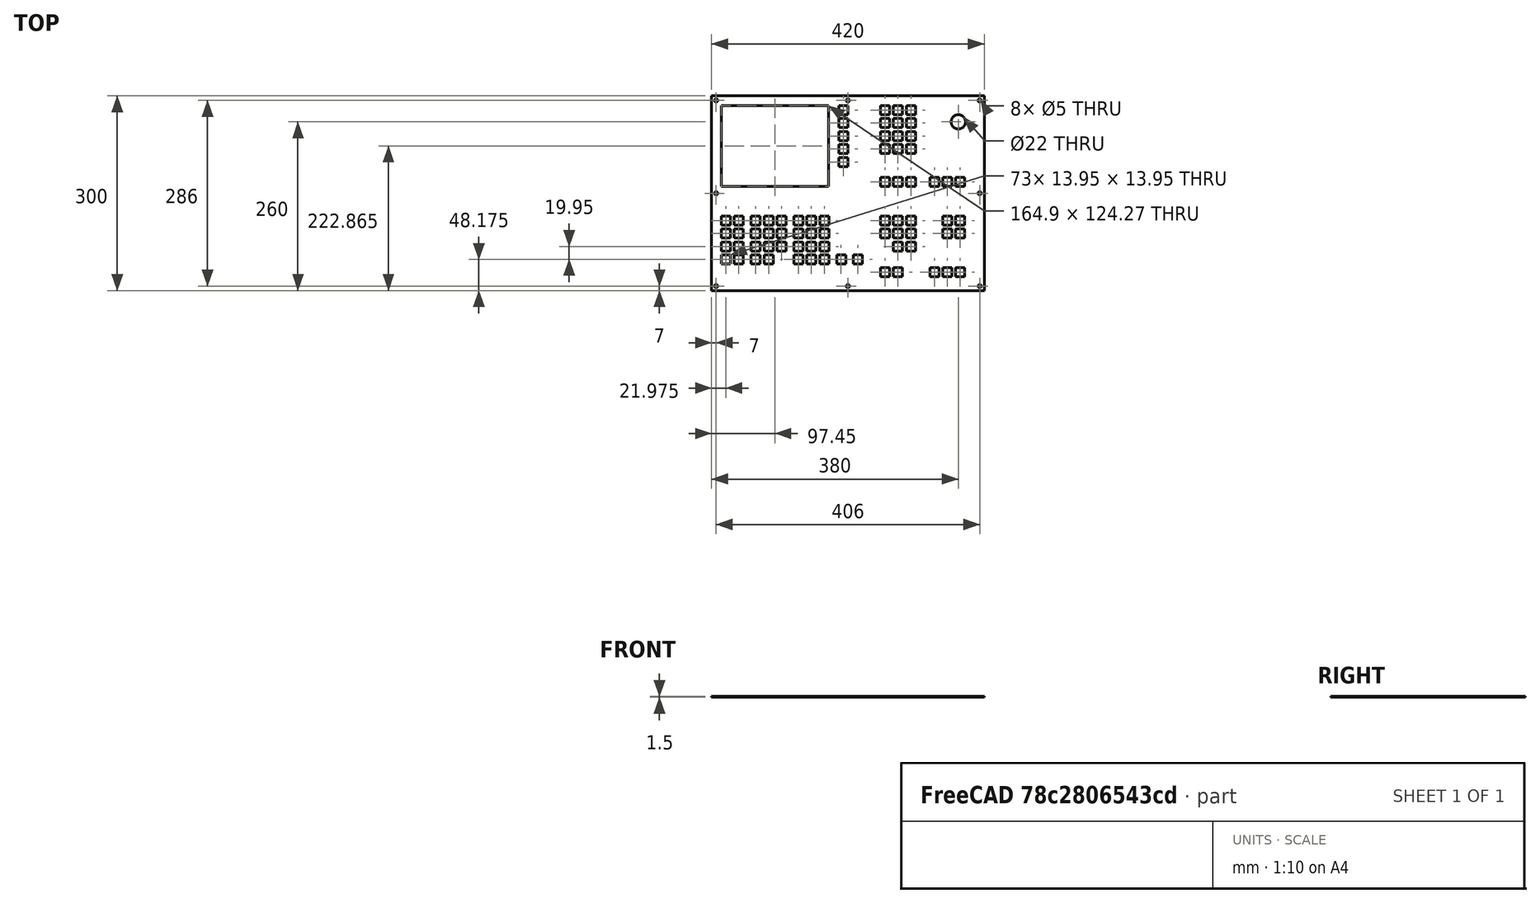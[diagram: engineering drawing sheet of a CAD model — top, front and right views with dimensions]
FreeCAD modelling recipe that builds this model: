
FCSTD DOCUMENT  (FreeCAD 0.20R26228 (Git))
Label: Hildi_Controller
License: All rights reserved
LicenseURL: http://en.wikipedia.org/wiki/All_rights_reserved
objects: Sketcher::SketchObject×1, Spreadsheet::Sheet×1, PartDesign::Pad×1, PartDesign::Body×1
note: 4 computed .brp shape members not serialized (recipe doc carries the construction recipe); baked Part::Feature solids carry a one-line shape summary decoded from their .brp

FEATURE [Sketcher::SketchObject] Sketch
  FullyConstrained = true
  MapMode = 5
  Support = -> [XY_Plane]
  expr: Constraints[229] = Spreadsheet.key_spacing
  expr: Constraints[421] = Spreadsheet.key_size
  expr: Constraints[445] = Spreadsheet.key_size
  expr: Constraints[417] = Spreadsheet.key_size
  expr: Constraints[439] = Spreadsheet.key_size
  expr: Constraints[416] = Spreadsheet.key_size
  expr: Constraints[625] = Spreadsheet.key_size
  expr: Constraints[169] = Spreadsheet.group_spacing
  expr: Constraints[440] = Spreadsheet.key_size
  expr: Constraints[450] = Spreadsheet.key_spacing
  expr: Constraints[414] = Spreadsheet.key_size
  expr: Constraints[219] = Spreadsheet.key_spacing
  expr: Constraints[144] = Spreadsheet.key_spacing
  expr: Constraints[626] = Spreadsheet.key_size
  expr: Constraints[415] = Spreadsheet.key_size
  expr: Constraints[220] = Spreadsheet.key_spacing
  expr: Constraints[230] = Spreadsheet.key_spacing
  expr: Constraints[865] = Spreadsheet.key_size
  expr: Constraints[624] = Spreadsheet.key_size
  expr: Constraints[285] = Spreadsheet.key_spacing
  expr: Constraints[443] = Spreadsheet.key_size
  expr: Constraints[278] = Spreadsheet.key_spacing
  expr: Constraints[233] = Spreadsheet.key_spacing
  expr: Constraints[442] = Spreadsheet.key_size
  expr: Constraints[769] = Spreadsheet.key_size
  expr: Constraints[299] = Spreadsheet.key_spacing
  expr: Constraints[915] = Spreadsheet.key_size
  expr: Constraints[623] = Spreadsheet.group_spacing
  expr: Constraints[493] = Spreadsheet.key_size
  expr: Constraints[300] = Spreadsheet.key_spacing
  expr: Constraints[494] = Spreadsheet.key_size
  expr: Constraints[444] = Spreadsheet.key_size
  expr: Constraints[446] = Spreadsheet.key_size
  expr: Constraints[221] = Spreadsheet.key_spacing
  expr: Constraints[635] = Spreadsheet.group_spacing
  expr: Constraints[143] = Spreadsheet.key_size
  expr: Constraints[422] = Spreadsheet.key_size
  expr: Constraints[567] = Spreadsheet.key_spacing
  expr: Constraints[218] = Spreadsheet.key_spacing
  expr: Constraints[566] = Spreadsheet.key_spacing
  expr: Constraints[639] = Spreadsheet.key_size
  expr: Constraints[418] = Spreadsheet.key_size
  expr: Constraints[863] = Spreadsheet.group_spacing
  expr: Constraints[495] = Spreadsheet.key_size
  expr: Constraints[922] = Spreadsheet.key_spacing
  expr: Constraints[780] = Spreadsheet.key_spacing
  expr: Constraints[441] = Spreadsheet.key_size
  expr: Constraints[496] = Spreadsheet.key_size
  expr: Constraints[925] = Spreadsheet.key_size
  sketch-geometry (309):
    g0: LineSegment StartX=-210 StartY=150 StartZ=0 EndX=210 EndY=150 EndZ=0
    g1: LineSegment StartX=210 StartY=150 StartZ=0 EndX=210 EndY=-150 EndZ=0
    g2: LineSegment StartX=210 StartY=-150 StartZ=0 EndX=-210 EndY=-150 EndZ=0
    g3: LineSegment StartX=-210 StartY=-150 StartZ=0 EndX=-210 EndY=150 EndZ=0
    g4: LineSegment StartX=-195 StartY=135 StartZ=0 EndX=-30.1 EndY=135 EndZ=0
    g5: LineSegment StartX=-30.1 StartY=135 StartZ=0 EndX=-30.1 EndY=10.73 EndZ=0
    g6: LineSegment StartX=-30.1 StartY=10.73 StartZ=0 EndX=-195 EndY=10.73 EndZ=0
    g7: LineSegment StartX=-195 StartY=10.73 StartZ=0 EndX=-195 EndY=135 EndZ=0
    g8: Circle CenterX=170 CenterY=110 CenterZ=0 NormalX=0 NormalY=0 NormalZ=1 AngleXU=0 Radius=11
    g9: LineSegment StartX=-195 StartY=-35 StartZ=0 EndX=-181.05 EndY=-35 EndZ=0
    g10: LineSegment StartX=-181.05 StartY=-35 StartZ=0 EndX=-181.05 EndY=-48.95 EndZ=0
    g11: LineSegment StartX=-181.05 StartY=-48.95 StartZ=0 EndX=-195 EndY=-48.95 EndZ=0
    g12: LineSegment StartX=-195 StartY=-48.95 StartZ=0 EndX=-195 EndY=-35 EndZ=0
    g13: LineSegment StartX=-195 StartY=-54.95 StartZ=0 EndX=-181.05 EndY=-54.95 EndZ=0
    g14: LineSegment StartX=-181.05 StartY=-54.95 StartZ=0 EndX=-181.05 EndY=-68.9 EndZ=0
    g15: LineSegment StartX=-181.05 StartY=-68.9 StartZ=0 EndX=-195 EndY=-68.9 EndZ=0
    g16: LineSegment StartX=-195 StartY=-68.9 StartZ=0 EndX=-195 EndY=-54.95 EndZ=0
    g17: LineSegment StartX=-195 StartY=-74.9 StartZ=0 EndX=-181.05 EndY=-74.9 EndZ=0
    g18: LineSegment StartX=-181.05 StartY=-74.9 StartZ=0 EndX=-181.05 EndY=-88.85 EndZ=0
    g19: LineSegment StartX=-181.05 StartY=-88.85 StartZ=0 EndX=-195 EndY=-88.85 EndZ=0
    g20: LineSegment StartX=-195 StartY=-88.85 StartZ=0 EndX=-195 EndY=-74.9 EndZ=0
    g21: LineSegment StartX=-195 StartY=-94.85 StartZ=0 EndX=-181.05 EndY=-94.85 EndZ=0
    g22: LineSegment StartX=-181.05 StartY=-94.85 StartZ=0 EndX=-181.05 EndY=-108.8 EndZ=0
    g23: LineSegment StartX=-181.05 StartY=-108.8 StartZ=0 EndX=-195 EndY=-108.8 EndZ=0
    g24: LineSegment StartX=-195 StartY=-108.8 StartZ=0 EndX=-195 EndY=-94.85 EndZ=0
    g25: LineSegment StartX=-175.05 StartY=-35 StartZ=0 EndX=-161.1 EndY=-35 EndZ=0
    g26: LineSegment StartX=-161.1 StartY=-35 StartZ=0 EndX=-161.1 EndY=-48.95 EndZ=0
    g27: LineSegment StartX=-161.1 StartY=-48.95 StartZ=0 EndX=-175.05 EndY=-48.95 EndZ=0
    g28: LineSegment StartX=-175.05 StartY=-48.95 StartZ=0 EndX=-175.05 EndY=-35 EndZ=0
    g29: LineSegment StartX=-175.05 StartY=-54.95 StartZ=0 EndX=-161.1 EndY=-54.95 EndZ=0
    g30: LineSegment StartX=-161.1 StartY=-54.95 StartZ=0 EndX=-161.1 EndY=-68.9 EndZ=0
    g31: LineSegment StartX=-161.1 StartY=-68.9 StartZ=0 EndX=-175.05 EndY=-68.9 EndZ=0
    g32: LineSegment StartX=-175.05 StartY=-68.9 StartZ=0 EndX=-175.05 EndY=-54.95 EndZ=0
    g33: LineSegment StartX=-175.05 StartY=-74.9 StartZ=0 EndX=-161.1 EndY=-74.9 EndZ=0
    g34: LineSegment StartX=-161.1 StartY=-74.9 StartZ=0 EndX=-161.1 EndY=-88.85 EndZ=0
    g35: LineSegment StartX=-161.1 StartY=-88.85 StartZ=0 EndX=-175.05 EndY=-88.85 EndZ=0
    g36: LineSegment StartX=-175.05 StartY=-88.85 StartZ=0 EndX=-175.05 EndY=-74.9 EndZ=0
    g37: LineSegment StartX=-175.05 StartY=-94.85 StartZ=0 EndX=-161.1 EndY=-94.85 EndZ=0
    g38: LineSegment StartX=-161.1 StartY=-94.85 StartZ=0 EndX=-161.1 EndY=-108.8 EndZ=0
    g39: LineSegment StartX=-161.1 StartY=-108.8 StartZ=0 EndX=-175.05 EndY=-108.8 EndZ=0
    g40: LineSegment StartX=-175.05 StartY=-108.8 StartZ=0 EndX=-175.05 EndY=-94.85 EndZ=0
    g41: LineSegment StartX=-149.1 StartY=-35 StartZ=0 EndX=-135.15 EndY=-35 EndZ=0
    g42: LineSegment StartX=-135.15 StartY=-35 StartZ=0 EndX=-135.15 EndY=-48.95 EndZ=0
    g43: LineSegment StartX=-135.15 StartY=-48.95 StartZ=0 EndX=-149.1 EndY=-48.95 EndZ=0
    g44: LineSegment StartX=-149.1 StartY=-48.95 StartZ=0 EndX=-149.1 EndY=-35 EndZ=0
    g45: LineSegment StartX=-129.15 StartY=-35 StartZ=0 EndX=-115.2 EndY=-35 EndZ=0
    g46: LineSegment StartX=-115.2 StartY=-35 StartZ=0 EndX=-115.2 EndY=-48.95 EndZ=0
    g47: LineSegment StartX=-115.2 StartY=-48.95 StartZ=0 EndX=-129.15 EndY=-48.95 EndZ=0
    g48: LineSegment StartX=-129.15 StartY=-48.95 StartZ=0 EndX=-129.15 EndY=-35 EndZ=0
    g49: LineSegment StartX=-149.1 StartY=-54.95 StartZ=0 EndX=-135.15 EndY=-54.95 EndZ=0
    g50: LineSegment StartX=-135.15 StartY=-54.95 StartZ=0 EndX=-135.15 EndY=-68.9 EndZ=0
    g51: LineSegment StartX=-135.15 StartY=-68.9 StartZ=0 EndX=-149.1 EndY=-68.9 EndZ=0
    g52: LineSegment StartX=-149.1 StartY=-68.9 StartZ=0 EndX=-149.1 EndY=-54.95 EndZ=0
    g53: LineSegment StartX=-129.15 StartY=-54.95 StartZ=0 EndX=-115.2 EndY=-54.95 EndZ=0
    g54: LineSegment StartX=-115.2 StartY=-54.95 StartZ=0 EndX=-115.2 EndY=-68.9 EndZ=0
    g55: LineSegment StartX=-115.2 StartY=-68.9 StartZ=0 EndX=-129.15 EndY=-68.9 EndZ=0
    g56: LineSegment StartX=-129.15 StartY=-68.9 StartZ=0 EndX=-129.15 EndY=-54.95 EndZ=0
    g57: LineSegment StartX=-109.2 StartY=-54.95 StartZ=0 EndX=-95.25 EndY=-54.95 EndZ=0
    g58: LineSegment StartX=-95.25 StartY=-54.95 StartZ=0 EndX=-95.25 EndY=-68.9 EndZ=0
    g59: LineSegment StartX=-95.25 StartY=-68.9 StartZ=0 EndX=-109.2 EndY=-68.9 EndZ=0
    g60: LineSegment StartX=-109.2 StartY=-68.9 StartZ=0 EndX=-109.2 EndY=-54.95 EndZ=0
    g61: LineSegment StartX=-149.1 StartY=-74.9 StartZ=0 EndX=-135.15 EndY=-74.9 EndZ=0
    g62: LineSegment StartX=-135.15 StartY=-74.9 StartZ=0 EndX=-135.15 EndY=-88.85 EndZ=0
    g63: LineSegment StartX=-135.15 StartY=-88.85 StartZ=0 EndX=-149.1 EndY=-88.85 EndZ=0
    g64: LineSegment StartX=-149.1 StartY=-88.85 StartZ=0 EndX=-149.1 EndY=-74.9 EndZ=0
    g65: LineSegment StartX=-129.15 StartY=-74.9 StartZ=0 EndX=-115.2 EndY=-74.9 EndZ=0
    g66: LineSegment StartX=-115.2 StartY=-74.9 StartZ=0 EndX=-115.2 EndY=-88.85 EndZ=0
    g67: LineSegment StartX=-115.2 StartY=-88.85 StartZ=0 EndX=-129.15 EndY=-88.85 EndZ=0
    g68: LineSegment StartX=-129.15 StartY=-88.85 StartZ=0 EndX=-129.15 EndY=-74.9 EndZ=0
    g69: LineSegment StartX=-109.2 StartY=-74.9 StartZ=0 EndX=-95.25 EndY=-74.9 EndZ=0
    g70: LineSegment StartX=-95.25 StartY=-74.9 StartZ=0 EndX=-95.25 EndY=-88.85 EndZ=0
    g71: LineSegment StartX=-95.25 StartY=-88.85 StartZ=0 EndX=-109.2 EndY=-88.85 EndZ=0
    g72: LineSegment StartX=-109.2 StartY=-88.85 StartZ=0 EndX=-109.2 EndY=-74.9 EndZ=0
    g73: LineSegment StartX=50 StartY=135 StartZ=0 EndX=63.95 EndY=135 EndZ=0
    g74: LineSegment StartX=63.95 StartY=135 StartZ=0 EndX=63.95 EndY=121.05 EndZ=0
    g75: LineSegment StartX=63.95 StartY=121.05 StartZ=0 EndX=50 EndY=121.05 EndZ=0
    g76: LineSegment StartX=50 StartY=121.05 StartZ=0 EndX=50 EndY=135 EndZ=0
    g77: LineSegment StartX=69.95 StartY=135 StartZ=0 EndX=83.9 EndY=135 EndZ=0
    g78: LineSegment StartX=83.9 StartY=135 StartZ=0 EndX=83.9 EndY=121.05 EndZ=0
    g79: LineSegment StartX=83.9 StartY=121.05 StartZ=0 EndX=69.95 EndY=121.05 EndZ=0
    g80: LineSegment StartX=69.95 StartY=121.05 StartZ=0 EndX=69.95 EndY=135 EndZ=0
    g81: LineSegment StartX=89.9 StartY=135 StartZ=0 EndX=103.85 EndY=135 EndZ=0
    g82: LineSegment StartX=103.85 StartY=135 StartZ=0 EndX=103.85 EndY=121.05 EndZ=0
    g83: LineSegment StartX=103.85 StartY=121.05 StartZ=0 EndX=89.9 EndY=121.05 EndZ=0
    g84: LineSegment StartX=89.9 StartY=121.05 StartZ=0 EndX=89.9 EndY=135 EndZ=0
    g85: LineSegment StartX=63.95 StartY=115.05 StartZ=0 EndX=50 EndY=115.05 EndZ=0
    g86: LineSegment StartX=50 StartY=115.05 StartZ=0 EndX=50 EndY=101.1 EndZ=0
    g87: LineSegment StartX=50 StartY=101.1 StartZ=0 EndX=63.95 EndY=101.1 EndZ=0
    g88: LineSegment StartX=63.95 StartY=101.1 StartZ=0 EndX=63.95 EndY=115.05 EndZ=0
    g89: LineSegment StartX=69.95 StartY=115.05 StartZ=0 EndX=83.9 EndY=115.05 EndZ=0
    g90: LineSegment StartX=83.9 StartY=115.05 StartZ=0 EndX=83.9 EndY=101.1 EndZ=0
    g91: LineSegment StartX=83.9 StartY=101.1 StartZ=0 EndX=69.95 EndY=101.1 EndZ=0
    g92: LineSegment StartX=69.95 StartY=101.1 StartZ=0 EndX=69.95 EndY=115.05 EndZ=0
    g93: LineSegment StartX=89.9 StartY=115.05 StartZ=0 EndX=103.85 EndY=115.05 EndZ=0
    g94: LineSegment StartX=103.85 StartY=115.05 StartZ=0 EndX=103.85 EndY=101.1 EndZ=0
    g95: LineSegment StartX=103.85 StartY=101.1 StartZ=0 EndX=89.9 EndY=101.1 EndZ=0
    g96: LineSegment StartX=89.9 StartY=101.1 StartZ=0 EndX=89.9 EndY=115.05 EndZ=0
    g97: LineSegment StartX=50 StartY=95.1 StartZ=0 EndX=63.95 EndY=95.1 EndZ=0
    g98: LineSegment StartX=63.95 StartY=95.1 StartZ=0 EndX=63.95 EndY=81.15 EndZ=0
    g99: LineSegment StartX=63.95 StartY=81.15 StartZ=0 EndX=50 EndY=81.15 EndZ=0
    g100: LineSegment StartX=50 StartY=81.15 StartZ=0 EndX=50 EndY=95.1 EndZ=0
    g101: LineSegment StartX=69.95 StartY=95.1 StartZ=0 EndX=83.9 EndY=95.1 EndZ=0
    g102: LineSegment StartX=83.9 StartY=95.1 StartZ=0 EndX=83.9 EndY=81.15 EndZ=0
    g103: LineSegment StartX=83.9 StartY=81.15 StartZ=0 EndX=69.95 EndY=81.15 EndZ=0
    g104: LineSegment StartX=69.95 StartY=81.15 StartZ=0 EndX=69.95 EndY=95.1 EndZ=0
    g105: LineSegment StartX=89.9 StartY=95.1 StartZ=0 EndX=103.85 EndY=95.1 EndZ=0
    g106: LineSegment StartX=103.85 StartY=95.1 StartZ=0 EndX=103.85 EndY=81.15 EndZ=0
    g107: LineSegment StartX=103.85 StartY=81.15 StartZ=0 EndX=89.9 EndY=81.15 EndZ=0
    g108: LineSegment StartX=89.9 StartY=81.15 StartZ=0 EndX=89.9 EndY=95.1 EndZ=0
    g109: LineSegment StartX=50 StartY=75.15 StartZ=0 EndX=63.95 EndY=75.15 EndZ=0
    g110: LineSegment StartX=63.95 StartY=75.15 StartZ=0 EndX=63.95 EndY=61.2 EndZ=0
    g111: LineSegment StartX=69.95 StartY=75.15 StartZ=0 EndX=83.9 EndY=75.15 EndZ=0
    g112: LineSegment StartX=83.9 StartY=75.15 StartZ=0 EndX=83.9 EndY=61.2 EndZ=0
    g113: LineSegment StartX=83.9 StartY=61.2 StartZ=0 EndX=69.95 EndY=61.2 EndZ=0
    g114: LineSegment StartX=69.95 StartY=61.2 StartZ=0 EndX=69.95 EndY=75.15 EndZ=0
    g115: LineSegment StartX=89.9 StartY=75.15 StartZ=0 EndX=103.85 EndY=75.15 EndZ=0
    g116: LineSegment StartX=103.85 StartY=75.15 StartZ=0 EndX=103.85 EndY=61.2 EndZ=0
    g117: LineSegment StartX=103.85 StartY=61.2 StartZ=0 EndX=89.9 EndY=61.2 EndZ=0
    g118: LineSegment StartX=89.9 StartY=61.2 StartZ=0 EndX=89.9 EndY=75.15 EndZ=0
    g119: LineSegment StartX=180 StartY=-114.8 StartZ=0 EndX=166.05 EndY=-114.8 EndZ=0
    g120: LineSegment StartX=166.05 StartY=-114.8 StartZ=0 EndX=166.05 EndY=-128.75 EndZ=0
    g121: LineSegment StartX=166.05 StartY=-128.75 StartZ=0 EndX=180 EndY=-128.75 EndZ=0
    g122: LineSegment StartX=180 StartY=-128.75 StartZ=0 EndX=180 EndY=-114.8 EndZ=0
    g123: LineSegment StartX=160.05 StartY=-114.8 StartZ=0 EndX=146.1 EndY=-114.8 EndZ=0
    g124: LineSegment StartX=146.1 StartY=-114.8 StartZ=0 EndX=146.1 EndY=-128.75 EndZ=0
    g125: LineSegment StartX=146.1 StartY=-128.75 StartZ=0 EndX=160.05 EndY=-128.75 EndZ=0
    g126: LineSegment StartX=160.05 StartY=-128.75 StartZ=0 EndX=160.05 EndY=-114.8 EndZ=0
    g127: LineSegment StartX=140.1 StartY=-114.8 StartZ=0 EndX=126.15 EndY=-114.8 EndZ=0
    g128: LineSegment StartX=126.15 StartY=-114.8 StartZ=0 EndX=126.15 EndY=-128.75 EndZ=0
    g129: LineSegment StartX=126.15 StartY=-128.75 StartZ=0 EndX=140.1 EndY=-128.75 EndZ=0
    g130: LineSegment StartX=140.1 StartY=-128.75 StartZ=0 EndX=140.1 EndY=-114.8 EndZ=0
    g131: LineSegment StartX=63.95 StartY=-48.95 StartZ=0 EndX=63.95 EndY=-35 EndZ=0
    g132: LineSegment StartX=63.95 StartY=-35 StartZ=0 EndX=50 EndY=-35 EndZ=0
    g133: LineSegment StartX=103.85 StartY=-54.95 StartZ=0 EndX=89.9 EndY=-54.95 EndZ=0
    g134: LineSegment StartX=89.9 StartY=-54.95 StartZ=0 EndX=89.9 EndY=-68.9 EndZ=0
    g135: LineSegment StartX=89.9 StartY=-68.9 StartZ=0 EndX=103.85 EndY=-68.9 EndZ=0
    g136: LineSegment StartX=103.85 StartY=-68.9 StartZ=0 EndX=103.85 EndY=-54.95 EndZ=0
    g137: LineSegment StartX=83.9 StartY=-54.95 StartZ=0 EndX=69.95 EndY=-54.95 EndZ=0
    g138: LineSegment StartX=69.95 StartY=-54.95 StartZ=0 EndX=69.95 EndY=-68.9 EndZ=0
    g139: LineSegment StartX=69.95 StartY=-68.9 StartZ=0 EndX=83.9 EndY=-68.9 EndZ=0
    g140: LineSegment StartX=83.9 StartY=-68.9 StartZ=0 EndX=83.9 EndY=-54.95 EndZ=0
    g141: LineSegment StartX=63.95 StartY=-54.95 StartZ=0 EndX=50 EndY=-54.95 EndZ=0
    g142: LineSegment StartX=50 StartY=-54.95 StartZ=0 EndX=50 EndY=-68.9 EndZ=0
    g143: LineSegment StartX=50 StartY=-68.9 StartZ=0 EndX=63.95 EndY=-68.9 EndZ=0
    g144: LineSegment StartX=63.95 StartY=-68.9 StartZ=0 EndX=63.95 EndY=-54.95 EndZ=0
    g145: LineSegment StartX=83.9 StartY=-48.95 StartZ=0 EndX=83.9 EndY=-35 EndZ=0
    g146: LineSegment StartX=83.9 StartY=-35 StartZ=0 EndX=69.95 EndY=-35 EndZ=0
    g147: LineSegment StartX=69.95 StartY=-74.9 StartZ=0 EndX=83.9 EndY=-74.9 EndZ=0
    g148: LineSegment StartX=83.9 StartY=-74.9 StartZ=0 EndX=83.9 EndY=-88.85 EndZ=0
    g149: LineSegment StartX=83.9 StartY=-88.85 StartZ=0 EndX=69.95 EndY=-88.85 EndZ=0
    g150: LineSegment StartX=69.95 StartY=-88.85 StartZ=0 EndX=69.95 EndY=-74.9 EndZ=0
    g151: LineSegment StartX=-17.4 StartY=-94.85 StartZ=0 EndX=-3.45 EndY=-94.85 EndZ=0
    g152: LineSegment StartX=-3.45 StartY=-94.85 StartZ=0 EndX=-3.45 EndY=-108.8 EndZ=0
    g153: LineSegment StartX=-3.45 StartY=-108.8 StartZ=0 EndX=-17.4 EndY=-108.8 EndZ=0
    g154: LineSegment StartX=-17.4 StartY=-108.8 StartZ=0 EndX=-17.4 EndY=-94.85 EndZ=0
    g155: Circle CenterX=-203 CenterY=143 CenterZ=0 NormalX=0 NormalY=0 NormalZ=1 AngleXU=0 Radius=2.5
    g156: Circle CenterX=-203 CenterY=0 CenterZ=0 NormalX=0 NormalY=0 NormalZ=1 AngleXU=0 Radius=2.5
    g157: Circle CenterX=-203 CenterY=-143 CenterZ=0 NormalX=0 NormalY=0 NormalZ=1 AngleXU=0 Radius=2.5
    g158: Circle CenterX=203 CenterY=-143 CenterZ=0 NormalX=0 NormalY=0 NormalZ=1 AngleXU=0 Radius=2.5
    g159: Circle CenterX=203 CenterY=0 CenterZ=0 NormalX=0 NormalY=0 NormalZ=1 AngleXU=0 Radius=2.5
    g160: Circle CenterX=203 CenterY=143 CenterZ=0 NormalX=0 NormalY=0 NormalZ=1 AngleXU=0 Radius=2.5
    g161: LineSegment StartX=89.9 StartY=-35 StartZ=0 EndX=103.85 EndY=-35 EndZ=0
    g162: LineSegment StartX=103.85 StartY=-35 StartZ=0 EndX=103.85 EndY=-48.95 EndZ=0
    g163: LineSegment StartX=103.85 StartY=-48.95 StartZ=0 EndX=89.9 EndY=-48.95 EndZ=0
    g164: LineSegment StartX=89.9 StartY=-48.95 StartZ=0 EndX=89.9 EndY=-35 EndZ=0
    g165: LineSegment StartX=89.9 StartY=-74.9 StartZ=0 EndX=103.85 EndY=-74.9 EndZ=0
    g166: LineSegment StartX=103.85 StartY=-74.9 StartZ=0 EndX=103.85 EndY=-88.85 EndZ=0
    g167: LineSegment StartX=103.85 StartY=-88.85 StartZ=0 EndX=89.9 EndY=-88.85 EndZ=0
    g168: LineSegment StartX=89.9 StartY=-88.85 StartZ=0 EndX=89.9 EndY=-74.9 EndZ=0
    g169: Circle CenterX=0 CenterY=-143 CenterZ=0 NormalX=0 NormalY=0 NormalZ=1 AngleXU=0 Radius=2.5
    g170: Circle CenterX=0 CenterY=143 CenterZ=0 NormalX=0 NormalY=0 NormalZ=1 AngleXU=0 Radius=2.5
    g171: LineSegment StartX=-129.15 StartY=-94.85 StartZ=0 EndX=-115.2 EndY=-94.85 EndZ=0
    g172: LineSegment StartX=-115.2 StartY=-94.85 StartZ=0 EndX=-115.2 EndY=-108.8 EndZ=0
    g173: LineSegment StartX=-115.2 StartY=-108.8 StartZ=0 EndX=-129.15 EndY=-108.8 EndZ=0
    g174: LineSegment StartX=-129.15 StartY=-108.8 StartZ=0 EndX=-129.15 EndY=-94.85 EndZ=0
    g175: LineSegment StartX=-109.2 StartY=-48.95 StartZ=0 EndX=-95.25 EndY=-48.95 EndZ=0
    g176: LineSegment StartX=-95.25 StartY=-48.95 StartZ=0 EndX=-95.25 EndY=-35 EndZ=0
    g177: LineSegment StartX=-95.25 StartY=-35 StartZ=0 EndX=-109.2 EndY=-35 EndZ=0
    g178: LineSegment StartX=-109.2 StartY=-35 StartZ=0 EndX=-109.2 EndY=-48.95 EndZ=0
    g179: LineSegment StartX=-149.1 StartY=-94.85 StartZ=0 EndX=-135.15 EndY=-94.85 EndZ=0
    g180: LineSegment StartX=-135.15 StartY=-94.85 StartZ=0 EndX=-135.15 EndY=-108.8 EndZ=0
    g181: LineSegment StartX=-135.15 StartY=-108.8 StartZ=0 EndX=-149.1 EndY=-108.8 EndZ=0
    g182: LineSegment StartX=-149.1 StartY=-108.8 StartZ=0 EndX=-149.1 EndY=-94.85 EndZ=0
    g183: LineSegment StartX=50 StartY=75.15 StartZ=0 EndX=50 EndY=61.2 EndZ=0
    g184: LineSegment StartX=50 StartY=61.2 StartZ=0 EndX=63.95 EndY=61.2 EndZ=0
    g185: LineSegment StartX=50 StartY=-35 StartZ=0 EndX=50 EndY=-48.95 EndZ=0
    g186: LineSegment StartX=50 StartY=-48.95 StartZ=0 EndX=63.95 EndY=-48.95 EndZ=0
    g187: LineSegment StartX=69.95 StartY=-35 StartZ=0 EndX=69.95 EndY=-48.95 EndZ=0
    g188: LineSegment StartX=69.95 StartY=-48.95 StartZ=0 EndX=83.9 EndY=-48.95 EndZ=0
    g189: LineSegment StartX=-83.25 StartY=-35 StartZ=0 EndX=-69.3 EndY=-35 EndZ=0
    g190: LineSegment StartX=-69.3 StartY=-35 StartZ=0 EndX=-69.3 EndY=-48.95 EndZ=0
    g191: LineSegment StartX=-69.3 StartY=-48.95 StartZ=0 EndX=-83.25 EndY=-48.95 EndZ=0
    g192: LineSegment StartX=-83.25 StartY=-48.95 StartZ=0 EndX=-83.25 EndY=-35 EndZ=0
    g193: LineSegment StartX=-63.3 StartY=-35 StartZ=0 EndX=-49.35 EndY=-35 EndZ=0
    g194: LineSegment StartX=-49.35 StartY=-35 StartZ=0 EndX=-49.35 EndY=-48.95 EndZ=0
    g195: LineSegment StartX=-49.35 StartY=-48.95 StartZ=0 EndX=-63.3 EndY=-48.95 EndZ=0
    g196: LineSegment StartX=-63.3 StartY=-48.95 StartZ=0 EndX=-63.3 EndY=-35 EndZ=0
    g197: LineSegment StartX=-83.25 StartY=-54.95 StartZ=0 EndX=-69.3 EndY=-54.95 EndZ=0
    g198: LineSegment StartX=-69.3 StartY=-54.95 StartZ=0 EndX=-69.3 EndY=-68.9 EndZ=0
    g199: LineSegment StartX=-69.3 StartY=-68.9 StartZ=0 EndX=-83.25 EndY=-68.9 EndZ=0
    g200: LineSegment StartX=-83.25 StartY=-68.9 StartZ=0 EndX=-83.25 EndY=-54.95 EndZ=0
    g201: LineSegment StartX=-63.3 StartY=-54.95 StartZ=0 EndX=-49.35 EndY=-54.95 EndZ=0
    g202: LineSegment StartX=-49.35 StartY=-54.95 StartZ=0 EndX=-49.35 EndY=-68.9 EndZ=0
    g203: LineSegment StartX=-49.35 StartY=-68.9 StartZ=0 EndX=-63.3 EndY=-68.9 EndZ=0
    g204: LineSegment StartX=-63.3 StartY=-68.9 StartZ=0 EndX=-63.3 EndY=-54.95 EndZ=0
    g205: LineSegment StartX=-43.35 StartY=-54.95 StartZ=0 EndX=-29.4 EndY=-54.95 EndZ=0
    g206: LineSegment StartX=-29.4 StartY=-54.95 StartZ=0 EndX=-29.4 EndY=-68.9 EndZ=0
    g207: LineSegment StartX=-29.4 StartY=-68.9 StartZ=0 EndX=-43.35 EndY=-68.9 EndZ=0
    g208: LineSegment StartX=-43.35 StartY=-68.9 StartZ=0 EndX=-43.35 EndY=-54.95 EndZ=0
    g209: LineSegment StartX=-83.25 StartY=-74.9 StartZ=0 EndX=-69.3 EndY=-74.9 EndZ=0
    g210: LineSegment StartX=-69.3 StartY=-74.9 StartZ=0 EndX=-69.3 EndY=-88.85 EndZ=0
    g211: LineSegment StartX=-69.3 StartY=-88.85 StartZ=0 EndX=-83.25 EndY=-88.85 EndZ=0
    g212: LineSegment StartX=-83.25 StartY=-88.85 StartZ=0 EndX=-83.25 EndY=-74.9 EndZ=0
    g213: LineSegment StartX=-63.3 StartY=-74.9 StartZ=0 EndX=-49.35 EndY=-74.9 EndZ=0
    g214: LineSegment StartX=-49.35 StartY=-74.9 StartZ=0 EndX=-49.35 EndY=-88.85 EndZ=0
    g215: LineSegment StartX=-49.35 StartY=-88.85 StartZ=0 EndX=-63.3 EndY=-88.85 EndZ=0
    g216: LineSegment StartX=-63.3 StartY=-88.85 StartZ=0 EndX=-63.3 EndY=-74.9 EndZ=0
    g217: LineSegment StartX=-43.35 StartY=-74.9 StartZ=0 EndX=-29.4 EndY=-74.9 EndZ=0
    g218: LineSegment StartX=-29.4 StartY=-74.9 StartZ=0 EndX=-29.4 EndY=-88.85 EndZ=0
    g219: LineSegment StartX=-29.4 StartY=-88.85 StartZ=0 EndX=-43.35 EndY=-88.85 EndZ=0
    g220: LineSegment StartX=-43.35 StartY=-88.85 StartZ=0 EndX=-43.35 EndY=-74.9 EndZ=0
    g221: LineSegment StartX=-63.3 StartY=-94.85 StartZ=0 EndX=-49.35 EndY=-94.85 EndZ=0
    g222: LineSegment StartX=-49.35 StartY=-94.85 StartZ=0 EndX=-49.35 EndY=-108.8 EndZ=0
    g223: LineSegment StartX=-49.35 StartY=-108.8 StartZ=0 EndX=-63.3 EndY=-108.8 EndZ=0
    g224: LineSegment StartX=-63.3 StartY=-108.8 StartZ=0 EndX=-63.3 EndY=-94.85 EndZ=0
    g225: LineSegment StartX=-43.35 StartY=-48.95 StartZ=0 EndX=-29.4 EndY=-48.95 EndZ=0
    g226: LineSegment StartX=-29.4 StartY=-48.95 StartZ=0 EndX=-29.4 EndY=-35 EndZ=0
    g227: LineSegment StartX=-29.4 StartY=-35 StartZ=0 EndX=-43.35 EndY=-35 EndZ=0
    g228: LineSegment StartX=-43.35 StartY=-35 StartZ=0 EndX=-43.35 EndY=-48.95 EndZ=0
    g229: LineSegment StartX=-83.25 StartY=-94.85 StartZ=0 EndX=-69.3 EndY=-94.85 EndZ=0
    g230: LineSegment StartX=-69.3 StartY=-94.85 StartZ=0 EndX=-69.3 EndY=-108.8 EndZ=0
    g231: LineSegment StartX=-69.3 StartY=-108.8 StartZ=0 EndX=-83.25 EndY=-108.8 EndZ=0
    g232: LineSegment StartX=-83.25 StartY=-108.8 StartZ=0 EndX=-83.25 EndY=-94.85 EndZ=0
    g233: LineSegment StartX=50 StartY=-114.8 StartZ=0 EndX=63.95 EndY=-114.8 EndZ=0
    g234: LineSegment StartX=63.95 StartY=-114.8 StartZ=0 EndX=63.95 EndY=-128.75 EndZ=0
    g235: LineSegment StartX=63.95 StartY=-128.75 StartZ=0 EndX=50 EndY=-128.75 EndZ=0
    g236: LineSegment StartX=50 StartY=-128.75 StartZ=0 EndX=50 EndY=-114.8 EndZ=0
    g237: LineSegment StartX=69.95 StartY=-114.8 StartZ=0 EndX=83.9 EndY=-114.8 EndZ=0
    g238: LineSegment StartX=83.9 StartY=-114.8 StartZ=0 EndX=83.9 EndY=-128.75 EndZ=0
    g239: LineSegment StartX=83.9 StartY=-128.75 StartZ=0 EndX=69.95 EndY=-128.75 EndZ=0
    g240: LineSegment StartX=69.95 StartY=-128.75 StartZ=0 EndX=69.95 EndY=-114.8 EndZ=0
    g241: LineSegment StartX=50 StartY=24.68 StartZ=0 EndX=63.95 EndY=24.68 EndZ=0
    g242: LineSegment StartX=63.95 StartY=24.68 StartZ=0 EndX=63.95 EndY=10.73 EndZ=0
    g243: LineSegment StartX=63.95 StartY=10.73 StartZ=0 EndX=50 EndY=10.73 EndZ=0
    g244: LineSegment StartX=50 StartY=10.73 StartZ=0 EndX=50 EndY=24.68 EndZ=0
    g245: LineSegment StartX=69.95 StartY=24.68 StartZ=0 EndX=83.9 EndY=24.68 EndZ=0
    g246: LineSegment StartX=83.9 StartY=24.68 StartZ=0 EndX=83.9 EndY=10.73 EndZ=0
    g247: LineSegment StartX=83.9 StartY=10.73 StartZ=0 EndX=69.95 EndY=10.73 EndZ=0
    g248: LineSegment StartX=69.95 StartY=10.73 StartZ=0 EndX=69.95 EndY=24.68 EndZ=0
    g249: LineSegment StartX=166.05 StartY=-68.9 StartZ=0 EndX=180 EndY=-68.9 EndZ=0
    g250: LineSegment StartX=180 StartY=-68.9 StartZ=0 EndX=180 EndY=-54.95 EndZ=0
    g251: LineSegment StartX=180 StartY=-54.95 StartZ=0 EndX=166.05 EndY=-54.95 EndZ=0
    g252: LineSegment StartX=166.05 StartY=-54.95 StartZ=0 EndX=166.05 EndY=-68.9 EndZ=0
    g253: LineSegment StartX=180 StartY=-35 StartZ=0 EndX=166.05 EndY=-35 EndZ=0
    g254: LineSegment StartX=166.05 StartY=-35 StartZ=0 EndX=166.05 EndY=-48.95 EndZ=0
    g255: LineSegment StartX=166.05 StartY=-48.95 StartZ=0 EndX=180 EndY=-48.95 EndZ=0
    g256: LineSegment StartX=180 StartY=-48.95 StartZ=0 EndX=180 EndY=-35 EndZ=0
    g257: LineSegment StartX=89.9 StartY=24.68 StartZ=0 EndX=103.85 EndY=24.68 EndZ=0
    g258: LineSegment StartX=103.85 StartY=24.68 StartZ=0 EndX=103.85 EndY=10.73 EndZ=0
    g259: LineSegment StartX=103.85 StartY=10.73 StartZ=0 EndX=89.9 EndY=10.73 EndZ=0
    g260: LineSegment StartX=89.9 StartY=10.73 StartZ=0 EndX=89.9 EndY=24.68 EndZ=0
    g261: LineSegment StartX=160.05 StartY=-35 StartZ=0 EndX=146.1 EndY=-35 EndZ=0
    g262: LineSegment StartX=146.1 StartY=-35 StartZ=0 EndX=146.1 EndY=-48.95 EndZ=0
    g263: LineSegment StartX=146.1 StartY=-48.95 StartZ=0 EndX=160.05 EndY=-48.95 EndZ=0
    g264: LineSegment StartX=160.05 StartY=-48.95 StartZ=0 EndX=160.05 EndY=-35 EndZ=0
    g265: LineSegment StartX=160.05 StartY=-54.95 StartZ=0 EndX=146.1 EndY=-54.95 EndZ=0
    g266: LineSegment StartX=146.1 StartY=-54.95 StartZ=0 EndX=146.1 EndY=-68.9 EndZ=0
    g267: LineSegment StartX=146.1 StartY=-68.9 StartZ=0 EndX=160.05 EndY=-68.9 EndZ=0
    g268: LineSegment StartX=160.05 StartY=-68.9 StartZ=0 EndX=160.05 EndY=-54.95 EndZ=0
    g269: LineSegment StartX=126.15 StartY=24.68 StartZ=0 EndX=140.1 EndY=24.68 EndZ=0
    g270: LineSegment StartX=140.1 StartY=24.68 StartZ=0 EndX=140.1 EndY=10.73 EndZ=0
    g271: LineSegment StartX=140.1 StartY=10.73 StartZ=0 EndX=126.15 EndY=10.73 EndZ=0
    g272: LineSegment StartX=126.15 StartY=10.73 StartZ=0 EndX=126.15 EndY=24.68 EndZ=0
    g273: LineSegment StartX=146.1 StartY=24.68 StartZ=0 EndX=160.05 EndY=24.68 EndZ=0
    g274: LineSegment StartX=160.05 StartY=24.68 StartZ=0 EndX=160.05 EndY=10.73 EndZ=0
    g275: LineSegment StartX=160.05 StartY=10.73 StartZ=0 EndX=146.1 EndY=10.73 EndZ=0
    g276: LineSegment StartX=146.1 StartY=10.73 StartZ=0 EndX=146.1 EndY=24.68 EndZ=0
    g277: LineSegment StartX=166.05 StartY=24.68 StartZ=0 EndX=180 EndY=24.68 EndZ=0
    g278: LineSegment StartX=180 StartY=24.68 StartZ=0 EndX=180 EndY=10.73 EndZ=0
    g279: LineSegment StartX=180 StartY=10.73 StartZ=0 EndX=166.05 EndY=10.73 EndZ=0
    g280: LineSegment StartX=166.05 StartY=10.73 StartZ=0 EndX=166.05 EndY=24.68 EndZ=0
    g281: LineSegment StartX=-43.35 StartY=-94.85 StartZ=0 EndX=-29.4 EndY=-94.85 EndZ=0
    g282: LineSegment StartX=-29.4 StartY=-94.85 StartZ=0 EndX=-29.4 EndY=-108.8 EndZ=0
    g283: LineSegment StartX=-29.4 StartY=-108.8 StartZ=0 EndX=-43.35 EndY=-108.8 EndZ=0
    g284: LineSegment StartX=-43.35 StartY=-108.8 StartZ=0 EndX=-43.35 EndY=-94.85 EndZ=0
    g285: LineSegment StartX=8.55 StartY=-94.85 StartZ=0 EndX=22.5 EndY=-94.85 EndZ=0
    g286: LineSegment StartX=22.5 StartY=-94.85 StartZ=0 EndX=22.5 EndY=-108.8 EndZ=0
    g287: LineSegment StartX=22.5 StartY=-108.8 StartZ=0 EndX=8.55 EndY=-108.8 EndZ=0
    g288: LineSegment StartX=8.55 StartY=-108.8 StartZ=0 EndX=8.55 EndY=-94.85 EndZ=0
    g289: LineSegment StartX=-13.95 StartY=135 StartZ=0 EndX=0 EndY=135 EndZ=0
    g290: LineSegment StartX=0 StartY=135 StartZ=0 EndX=0 EndY=121.05 EndZ=0
    g291: LineSegment StartX=0 StartY=121.05 StartZ=0 EndX=-13.95 EndY=121.05 EndZ=0
    g292: LineSegment StartX=-13.95 StartY=121.05 StartZ=0 EndX=-13.95 EndY=135 EndZ=0
    g293: LineSegment StartX=-13.95 StartY=115.05 StartZ=0 EndX=0 EndY=115.05 EndZ=0
    g294: LineSegment StartX=0 StartY=115.05 StartZ=0 EndX=0 EndY=101.1 EndZ=0
    g295: LineSegment StartX=0 StartY=101.1 StartZ=0 EndX=-13.95 EndY=101.1 EndZ=0
    g296: LineSegment StartX=-13.95 StartY=101.1 StartZ=0 EndX=-13.95 EndY=115.05 EndZ=0
    g297: LineSegment StartX=-13.95 StartY=95.1 StartZ=0 EndX=0 EndY=95.1 EndZ=0
    g298: LineSegment StartX=0 StartY=95.1 StartZ=0 EndX=0 EndY=81.15 EndZ=0
    g299: LineSegment StartX=0 StartY=81.15 StartZ=0 EndX=-13.95 EndY=81.15 EndZ=0
    g300: LineSegment StartX=-13.95 StartY=81.15 StartZ=0 EndX=-13.95 EndY=95.1 EndZ=0
    g301: LineSegment StartX=-13.95 StartY=75.15 StartZ=0 EndX=0 EndY=75.15 EndZ=0
    g302: LineSegment StartX=0 StartY=75.15 StartZ=0 EndX=0 EndY=61.2 EndZ=0
    g303: LineSegment StartX=0 StartY=61.2 StartZ=0 EndX=-13.95 EndY=61.2 EndZ=0
    g304: LineSegment StartX=-13.95 StartY=61.2 StartZ=0 EndX=-13.95 EndY=75.15 EndZ=0
    g305: LineSegment StartX=-13.95 StartY=55.2 StartZ=0 EndX=0 EndY=55.2 EndZ=0
    g306: LineSegment StartX=0 StartY=55.2 StartZ=0 EndX=0 EndY=41.25 EndZ=0
    g307: LineSegment StartX=0 StartY=41.25 StartZ=0 EndX=-13.95 EndY=41.25 EndZ=0
    g308: LineSegment StartX=-13.95 StartY=41.25 StartZ=0 EndX=-13.95 EndY=55.2 EndZ=0
  constraints (926):
    c: Coincident(g1,g2)
    c: Coincident(g2,g3)
    c: Coincident(g3,g0)
    c: DistanceY(g3,g3) = 300
    c: Coincident(g4,g5)
    c: Coincident(g5,g6)
    c: DistanceX(g4,g4) = 164.9
    c: DistanceY(g7,g7) = 124.27
    c: DistanceY(g4,g0) = 15
    c: Diameter(g8) = 22
    c: DistanceX(g8,g0) = 40
    c: DistanceY(g8,g0) = 40
    c: Coincident(g10,g11)
    c: Coincident(g11,g12)
    c: Coincident(g12,g9)
    c: Coincident(g13,g14)
    c: Coincident(g14,g15)
    c: Coincident(g15,g16)
    c: Coincident(g16,g13)
    c: Coincident(g17,g18)
    c: Coincident(g18,g19)
    c: Coincident(g19,g20)
    c: Coincident(g20,g17)
    c: Coincident(g21,g22)
    c: Coincident(g22,g23)
    c: Coincident(g23,g24)
    c: Coincident(g24,g21)
    c: Coincident(g25,g26)
    c: Coincident(g26,g27)
    c: Coincident(g29,g30)
    c: Coincident(g30,g31)
    c: Coincident(g31,g32)
    c: Coincident(g32,g29)
    c: Coincident(g33,g34)
    c: Coincident(g34,g35)
    c: Coincident(g35,g36)
    c: Coincident(g36,g33)
    c: Coincident(g37,g38)
    c: Coincident(g38,g39)
    c: Coincident(g39,g40)
    c: Coincident(g40,g37)
    c: Coincident(g42,g43)
    c: Coincident(g43,g44)
    c: Coincident(g44,g41)
    c: Coincident(g45,g46)
    c: Coincident(g46,g47)
    c: Coincident(g47,g48)
    c: Coincident(g48,g45)
    c: Coincident(g49,g50)
    c: Coincident(g50,g51)
    c: Coincident(g51,g52)
    c: Coincident(g52,g49)
    c: Coincident(g53,g54)
    c: Coincident(g54,g55)
    c: Coincident(g57,g58)
    c: Coincident(g58,g59)
    c: Coincident(g59,g60)
    c: Coincident(g60,g57)
    c: Coincident(g61,g62)
    c: Coincident(g62,g63)
    c: Coincident(g63,g64)
    c: Coincident(g64,g61)
    c: Coincident(g66,g67)
    c: Coincident(g67,g68)
    c: Coincident(g68,g65)
    c: Coincident(g70,g71)
    c: Coincident(g73,g74)
    c: Coincident(g74,g75)
    c: Coincident(g75,g76)
    c: Coincident(g76,g73)
    c: Coincident(g77,g78)
    c: Coincident(g78,g79)
    c: Coincident(g79,g80)
    c: Coincident(g80,g77)
    c: Coincident(g81,g82)
    c: Coincident(g82,g83)
    c: Coincident(g83,g84)
    c: Coincident(g84,g81)
    c: Coincident(g85,g86)
    c: Coincident(g86,g87)
    c: Coincident(g87,g88)
    c: Coincident(g88,g85)
    c: Coincident(g89,g90)
    c: Coincident(g90,g91)
    c: Coincident(g91,g92)
    c: Coincident(g92,g89)
    c: Coincident(g93,g94)
    c: Coincident(g94,g95)
    c: Coincident(g95,g96)
    c: Coincident(g96,g93)
    c: Coincident(g97,g98)
    c: Coincident(g98,g99)
    c: Coincident(g99,g100)
    c: Coincident(g100,g97)
    c: Coincident(g101,g102)
    c: Coincident(g102,g103)
    c: Coincident(g103,g104)
    c: Coincident(g105,g106)
    c: Coincident(g106,g107)
    c: Coincident(g107,g108)
    c: Coincident(g108,g105)
    c: Coincident(g109,g110)
    c: Coincident(g111,g112)
    c: Coincident(g112,g113)
    c: Coincident(g113,g114)
    c: Coincident(g114,g111)
    c: Coincident(g115,g116)
    c: Coincident(g116,g117)
    c: Coincident(g117,g118)
    c: Coincident(g118,g115)
    c: Coincident(g119,g120)
    c: Coincident(g120,g121)
    c: Coincident(g121,g122)
    c: Coincident(g122,g119)
    c: Coincident(g123,g124)
    c: Coincident(g124,g125)
    c: Coincident(g125,g126)
    c: Coincident(g126,g123)
    c: Coincident(g127,g128)
    c: Coincident(g128,g129)
    c: Coincident(g129,g130)
    c: Coincident(g130,g127)
    c: Coincident(g131,g132)
    c: Coincident(g133,g134)
    c: Coincident(g134,g135)
    c: Coincident(g135,g136)
    c: Coincident(g136,g133)
    c: Coincident(g137,g138)
    c: Coincident(g138,g139)
    c: Coincident(g139,g140)
    c: Coincident(g140,g137)
    c: Coincident(g141,g142)
    c: Coincident(g142,g143)
    c: Coincident(g143,g144)
    c: Coincident(g144,g141)
    c: Coincident(g145,g146)
    c: Coincident(g147,g148)
    c: Coincident(g148,g149)
    c: Coincident(g149,g150)
    c: Coincident(g150,g147)
    c: Coincident(g152,g153)
    c: Coincident(g153,g154)
    c: Coincident(g154,g151)
    c: DistanceY(g12,g12) = 13.95
    c: DistanceY(g13,g11) = 6
    c: DistanceX(g0,g155) = 7
    c: DistanceY(g155,g0) = 7
    c: Diameter(g155) = 5
    c: Coincident(g161,g162)
    c: Coincident(g162,g163)
    c: Coincident(g163,g164)
    c: Coincident(g164,g161)
    c: Coincident(g165,g166)
    c: Coincident(g166,g167)
    c: Coincident(g167,g168)
    c: Coincident(g168,g165)
    c: DistanceY(g2,g157) = 7
    c: DistanceX(g160,g0) = 7
    c: Coincident(g171,g172)
    c: Coincident(g172,g173)
    c: Coincident(g173,g174)
    c: Coincident(g174,g171)
    c: Coincident(g175,g176)
    c: Coincident(g176,g177)
    c: Coincident(g177,g178)
    c: Coincident(g178,g175)
    c: Coincident(g72,g69)
    c: Coincident(g66,g65)
    c: Coincident(g25,g28)
    c: DistanceX(g25,g41) = 12
    c: Coincident(g27,g28)
    c: Coincident(g70,g69)
    c: Coincident(g72,g71)
    c: Coincident(g152,g151)
    c: Coincident(g42,g41)
    c: Coincident(g10,g9)
    c: DistanceX(g0,g0) = 420
    c: Coincident(g179,g180)
    c: Coincident(g180,g181)
    c: Coincident(g181,g182)
    c: Coincident(g182,g179)
    c: Horizontal(g9)
    c: Horizontal(g25)
    c: Horizontal(g41)
    c: Horizontal(g45)
    c: Horizontal(g177)
    c: Horizontal(g0)
    c: Horizontal(g2)
    c: Horizontal(g13)
    c: Horizontal(g29)
    c: Horizontal(g49)
    c: Horizontal(g53)
    c: Horizontal(g57)
    c: Horizontal(g17)
    c: Horizontal(g33)
    c: Horizontal(g61)
    c: Horizontal(g65)
    c: Horizontal(g69)
    c: Horizontal(g21)
    c: Horizontal(g37)
    c: Horizontal(g171)
    c: Horizontal(g179)
    c: Vertical(g12)
    c: Vertical(g16)
    c: Vertical(g20)
    c: Vertical(g24)
    c: Vertical(g28)
    c: Vertical(g32)
    c: Vertical(g44)
    c: Vertical(g52)
    c: Vertical(g64)
    c: Vertical(g182)
    c: Vertical(g48)
    c: Vertical(g56)
    c: Vertical(g68)
    c: Vertical(g174)
    c: Vertical(g60)
    c: Vertical(g178)
    c: DistanceX(g41,g45) = 6
    c: DistanceX(g45,g177) = 6
    c: DistanceY(g17,g15) = 6
    c: DistanceY(g21,g19) = 6
    c: Horizontal(g4)
    c: Horizontal(g6)
    c: Vertical(g5)
    c: Vertical(g7)
    c: Vertical(g3)
    c: Vertical(g1)
    c: Horizontal(g81)
    c: DistanceX(g73,g77) = 6
    c: DistanceX(g77,g81) = 6
    c: Vertical(g76)
    c: Vertical(g86)
    c: DistanceY(g85,g75) = 6
    c: Horizontal(g73,g4)
    c: Vertical(g75,g85)
    c: Vertical(g180)
    c: Vertical(g11,g13)
    c: Vertical(g15,g17)
    c: Vertical(g19,g21)
    c: Vertical(g27,g29)
    c: Vertical(g31,g33)
    c: Vertical(g35,g37)
    c: Vertical(g43,g49)
    c: Vertical(g51,g61)
    c: Vertical(g63,g179)
    c: Vertical(g47,g53)
    c: Vertical(g55,g65)
    c: Vertical(g67,g171)
    c: Vertical(g175,g57)
    c: Vertical(g59,g69)
    c: Horizontal(g9,g25)
    c: Horizontal(g25,g41)
    c: Horizontal(g41,g45)
    c: Horizontal(g45,g177)
    c: Horizontal(g13,g29)
    c: Horizontal(g29,g49)
    c: Horizontal(g49,g53)
    c: Horizontal(g53,g57)
    c: Horizontal(g17,g33)
    c: Horizontal(g33,g61)
    c: Horizontal(g61,g65)
    c: Horizontal(g65,g69)
    c: Horizontal(g21,g37)
    c: Horizontal(g37,g179)
    c: Horizontal(g179,g171)
    c: Vertical(g78)
    c: Horizontal(g97)
    c: Horizontal(g109)
    c: Vertical(g86,g97)
    c: Vertical(g99,g109)
    c: Horizontal(g85,g89)
    c: Horizontal(g89,g93)
    c: Horizontal(g89)
    c: Horizontal(g107)
    c: Vertical(g94)
    c: Vertical(g110)
    c: Vertical(g118)
    c: DistanceY(g97,g86) = 6
    c: Vertical(g79,g89)
    c: Vertical(g91,g101)
    c: Vertical(g103,g111)
    c: Vertical(g83,g93)
    c: Vertical(g95,g105)
    c: Vertical(g107,g115)
    c: DistanceY(g109,g99) = 6
    c: Horizontal(g97,g101)
    c: Horizontal(g111,g109)
    c: Horizontal(g105,g101)
    c: Horizontal(g115,g111)
    c: Vertical(g155,g156)
    c: Vertical(g156,g157)
    c: Vertical(g160,g159)
    c: Vertical(g159,g158)
    c: Horizontal(g119)
    c: Vertical(g120)
    c: Vertical(g128)
    c: Horizontal(g127,g123)
    c: Horizontal(g123,g119)
    c: DistanceX(g127,g123) = 6
    c: DistanceX(g123,g119) = 6
    c: Horizontal(g141)
    c: Horizontal(g137)
    c: Horizontal(g147)
    c: Horizontal(g133)
    c: Horizontal(g161)
    c: Horizontal(g165)
    c: Vertical(g162)
    c: Vertical(g134)
    c: Vertical(g138)
    c: Vertical(g142)
    c: Vertical(g166)
    c: Coincident(g56,g53)
    c: Coincident(g55,g56)
    c: Coincident(g0,g1)
    c: Symmetric(g0,g1,g-1)
    c: DistanceX(g0,g7) = 15
    c: Coincident(g4,g7)
    c: Coincident(g6,g7)
    c: Vertical(g9,g6)
    c: DistanceY(g9,g-1) = 35
    c: DistanceX(g-1,g73) = 50
    c: Coincident(g104,g101)
    c: Horizontal(g73,g77)
    c: Horizontal(g77,g81)
    c: PointOnObject(g159,g-1)
    c: PointOnObject(g156,g-1)
    c: Horizontal(g171,g151)
    c: Horizontal(g151)
    c: Vertical(g183)
    c: Coincident(g184,g183)
    c: Coincident(g184,g110)
    c: Horizontal(g184)
    c: Coincident(g132,g185)
    c: Vertical(g185)
    c: Coincident(g185,g186)
    c: Coincident(g186,g131)
    c: Horizontal(g186)
    c: Horizontal(g132)
    c: Horizontal(g57,g137)
    c: Coincident(g146,g187)
    c: Vertical(g187)
    c: Coincident(g187,g188)
    c: Coincident(g188,g145)
    c: Horizontal(g188)
    c: Vertical(g98)
    c: Vertical(g102)
    c: Vertical(g106)
    c: Vertical(g108)
    c: Horizontal(g27)
    c: Horizontal(g31)
    c: Horizontal(g35)
    c: Horizontal(g39)
    c: Horizontal(g173)
    c: Horizontal(g181)
    c: Horizontal(g23)
    c: Horizontal(g71)
    c: Horizontal(g59)
    c: Horizontal(g43)
    c: Horizontal(g51)
    c: Horizontal(g63)
    c: Horizontal(g19)
    c: Horizontal(g15)
    c: Vertical(g58)
    c: Vertical(g70)
    c: Vertical(g66)
    c: Vertical(g54)
    c: Vertical(g50)
    c: Vertical(g62)
    c: Vertical(g172)
    c: Vertical(g22)
    c: Vertical(g38)
    c: Vertical(g40)
    c: Vertical(g18)
    c: Vertical(g34)
    c: Vertical(g36)
    c: Vertical(g30)
    c: Vertical(g14)
    c: Vertical(g176)
    c: Vertical(g46)
    c: Vertical(g42)
    c: Vertical(g26)
    c: Vertical(g10)
    c: Horizontal(g47)
    c: Horizontal(g73)
    c: Horizontal(g75)
    c: Horizontal(g85)
    c: Horizontal(g87)
    c: Horizontal(g99)
    c: Horizontal(g91)
    c: Horizontal(g101)
    c: Horizontal(g103)
    c: Horizontal(g111)
    c: Vertical(g114)
    c: Vertical(g104)
    c: Vertical(g88)
    c: Vertical(g90)
    c: Vertical(g92)
    c: Vertical(g96)
    c: Horizontal(g77)
    c: Horizontal(g79)
    c: Horizontal(g83)
    c: Horizontal(g93)
    c: Horizontal(g95)
    c: Horizontal(g105)
    c: Horizontal(g115)
    c: Horizontal(g117)
    c: Vertical(g116)
    c: Vertical(g112)
    c: Vertical(g100)
    c: Vertical(g74)
    c: Vertical(g80)
    c: Vertical(g84)
    c: Vertical(g82)
    c: DistanceY(g76,g76) = 13.95
    c: DistanceX(g73,g73) = 13.95
    c: DistanceX(g77,g77) = 13.95
    c: DistanceX(g81,g81) = 13.95
    c: DistanceY(g86,g86) = 13.95
    c: Horizontal(g79,g74)
    c: Horizontal(g78,g83)
    c: DistanceY(g100,g100) = 13.95
    c: DistanceY(g183,g183) = 13.95
    c: Vertical(g85,g74)
    c: Vertical(g87,g97)
    c: Vertical(g98,g109)
    c: Horizontal(g87,g91)
    c: Horizontal(g98,g103)
    c: Horizontal(g110,g113)
    c: Vertical(g78,g89)
    c: Vertical(g90,g101)
    c: Vertical(g102,g111)
    c: Horizontal(g90,g95)
    c: Horizontal(g102,g107)
    c: Horizontal(g112,g117)
    c: Vertical(g82,g93)
    c: Vertical(g94,g105)
    c: Vertical(g106,g115)
    c: Horizontal(g113)
    c: DistanceY(g16,g16) = 13.95
    c: DistanceY(g20,g20) = 13.95
    c: DistanceY(g24,g24) = 13.95
    c: DistanceX(g9,g9) = 13.95
    c: DistanceX(g25,g25) = 13.95
    c: DistanceX(g41,g41) = 13.95
    c: DistanceX(g45,g45) = 13.95
    c: DistanceX(g177,g177) = 13.95
    c: Horizontal(g175)
    c: Vertical(g72)
    c: Horizontal(g11)
    c: DistanceX(g9,g25) = 6
    c: Horizontal(g10,g27)
    c: Horizontal(g26,g43)
    c: Horizontal(g42,g47)
    c: Horizontal(g46,g175)
    c: Vertical(g10,g13)
    c: Vertical(g26,g29)
    c: Vertical(g42,g49)
    c: Vertical(g46,g53)
    c: Vertical(g175,g57)
    c: Horizontal(g14,g31)
    c: Horizontal(g30,g51)
    c: Horizontal(g50,g55)
    c: Horizontal(g54,g59)
    c: Horizontal(g55)
    c: Vertical(g14,g17)
    c: Vertical(g30,g33)
    c: Vertical(g50,g61)
    c: Vertical(g54,g65)
    c: Vertical(g58,g69)
    c: Horizontal(g18,g35)
    c: Horizontal(g34,g63)
    c: Horizontal(g62,g67)
    c: Horizontal(g66,g71)
    c: Vertical(g66,g171)
    c: Vertical(g18,g21)
    c: Vertical(g34,g37)
    c: Vertical(g62,g179)
    c: Horizontal(g67)
    c: Horizontal(g22,g39)
    c: Horizontal(g38,g181)
    c: Horizontal(g180,g173)
    c: Horizontal(g127)
    c: Horizontal(g129)
    c: Horizontal(g123)
    c: Horizontal(g125)
    c: Horizontal(g121)
    c: Vertical(g130)
    c: Vertical(g124)
    c: Vertical(g126)
    c: Vertical(g122)
    c: Horizontal(g129,g124)
    c: Horizontal(g125,g120)
    c: DistanceX(g127,g127) = 13.95
    c: DistanceX(g123,g123) = 13.95
    c: DistanceX(g119,g119) = 13.95
    c: DistanceY(g128,g128) = 13.95
    c: Vertical(g183,g132)
    c: Horizontal(g146)
    c: Horizontal(g163)
    c: Vertical(g145)
    c: Vertical(g164)
    c: Vertical(g131)
    c: Coincident(g190,g191)
    c: Coincident(g191,g192)
    c: Coincident(g192,g189)
    c: Coincident(g193,g194)
    c: Coincident(g194,g195)
    c: Coincident(g195,g196)
    c: Coincident(g196,g193)
    c: Coincident(g197,g198)
    c: Coincident(g198,g199)
    c: Coincident(g199,g200)
    c: Coincident(g200,g197)
    c: Coincident(g201,g202)
    c: Coincident(g202,g203)
    c: Coincident(g205,g206)
    c: Coincident(g206,g207)
    c: Coincident(g207,g208)
    c: Coincident(g208,g205)
    c: Coincident(g209,g210)
    c: Coincident(g210,g211)
    c: Coincident(g211,g212)
    c: Coincident(g212,g209)
    c: Coincident(g214,g215)
    c: Coincident(g215,g216)
    c: Coincident(g216,g213)
    c: Coincident(g218,g219)
    c: Coincident(g221,g222)
    c: Coincident(g222,g223)
    c: Coincident(g223,g224)
    c: Coincident(g224,g221)
    c: Coincident(g225,g226)
    c: Coincident(g226,g227)
    c: Coincident(g227,g228)
    c: Coincident(g228,g225)
    c: Coincident(g220,g217)
    c: Coincident(g214,g213)
    c: Coincident(g218,g217)
    c: Coincident(g220,g219)
    c: Coincident(g190,g189)
    c: Coincident(g229,g230)
    c: Coincident(g230,g231)
    c: Coincident(g231,g232)
    c: Coincident(g232,g229)
    c: Horizontal(g189)
    c: Horizontal(g193)
    c: Horizontal(g227)
    c: Horizontal(g197)
    c: Horizontal(g201)
    c: Horizontal(g205)
    c: Horizontal(g209)
    c: Horizontal(g213)
    c: Horizontal(g217)
    c: Horizontal(g221)
    c: Horizontal(g229)
    c: Vertical(g192)
    c: Vertical(g200)
    c: Vertical(g212)
    c: Vertical(g232)
    c: Vertical(g196)
    c: Vertical(g204)
    c: Vertical(g216)
    c: Vertical(g224)
    c: Vertical(g208)
    c: Vertical(g228)
    c: DistanceX(g189,g193) = 6
    c: DistanceX(g193,g227) = 6
    c: Vertical(g230)
    c: Vertical(g191,g197)
    c: Vertical(g199,g209)
    c: Vertical(g211,g229)
    c: Vertical(g195,g201)
    c: Vertical(g203,g213)
    c: Vertical(g215,g221)
    c: Vertical(g225,g205)
    c: Vertical(g207,g217)
    c: Horizontal(g189,g193)
    c: Horizontal(g193,g227)
    c: Horizontal(g197,g201)
    c: Horizontal(g201,g205)
    c: Horizontal(g209,g213)
    c: Horizontal(g213,g217)
    c: Horizontal(g229,g221)
    c: Coincident(g204,g201)
    c: Coincident(g203,g204)
    c: Horizontal(g223)
    c: Horizontal(g231)
    c: Horizontal(g219)
    c: Horizontal(g207)
    c: Horizontal(g191)
    c: Horizontal(g199)
    c: Horizontal(g211)
    c: Vertical(g206)
    c: Vertical(g218)
    c: Vertical(g214)
    c: Vertical(g202)
    c: Vertical(g198)
    c: Vertical(g210)
    c: Vertical(g222)
    c: Vertical(g226)
    c: Vertical(g194)
    c: Vertical(g190)
    c: Horizontal(g195)
    c: Horizontal(g225)
    c: Vertical(g220)
    c: Horizontal(g190,g195)
    c: Horizontal(g194,g225)
    c: Vertical(g190,g197)
    c: Vertical(g194,g201)
    c: Vertical(g225,g205)
    c: Horizontal(g198,g203)
    c: Horizontal(g202,g207)
    c: Horizontal(g203)
    c: Vertical(g198,g209)
    c: Vertical(g202,g213)
    c: Vertical(g206,g217)
    c: Horizontal(g210,g215)
    c: Horizontal(g214,g219)
    c: Vertical(g214,g221)
    c: Vertical(g210,g229)
    c: Horizontal(g215)
    c: Horizontal(g230,g223)
    c: DistanceX(g176,g189) = 12
    c: DistanceX(g189,g189) = 13.95
    c: DistanceX(g193,g193) = 13.95
    c: DistanceX(g227,g227) = 13.95
    c: Horizontal(g176,g189)
    c: Horizontal(g175,g191)
    c: Horizontal(g57,g197)
    c: Horizontal(g58,g199)
    c: Horizontal(g69,g209)
    c: Horizontal(g70,g211)
    c: Horizontal(g171,g229)
    c: Horizontal(g172,g231)
    c: DistanceX(g218,g151) = 12
    c: Vertical(g152)
    c: Vertical(g154)
    c: Horizontal(g153)
    c: DistanceX(g151,g151) = 13.95
    c: Horizontal(g153,g222)
    c: Vertical(g110,g131)
    c: Vertical(g146,g113)
    c: Vertical(g145,g112)
    c: Vertical(g161,g117)
    c: Vertical(g116,g161)
    c: Horizontal(g131,g146)
    c: Horizontal(g145,g161)
    c: Horizontal(g225,g185)
    c: Horizontal(g132,g226)
    c: Horizontal(g131,g187)
    c: Horizontal(g145,g163)
    c: Horizontal(g139)
    c: Vertical(g140)
    c: Vertical(g137,g187)
    c: Vertical(g137,g145)
    c: Horizontal(g138,g206)
    c: Horizontal(g133,g137)
    c: Vertical(g133,g163)
    c: Horizontal(g134,g139)
    c: Horizontal(g135)
    c: Vertical(g136)
    c: Vertical(g162,g133)
    c: Vertical(g185,g141)
    c: Vertical(g141,g131)
    c: Horizontal(g141,g205)
    c: Vertical(g144)
    c: Horizontal(g143)
    c: Horizontal(g206,g142)
    c: Vertical(g168)
    c: Vertical(g148)
    c: Vertical(g150)
    c: Horizontal(g149)
    c: Horizontal(g167)
    c: Horizontal(g217,g147)
    c: Vertical(g147,g138)
    c: Vertical(g139,g147)
    c: Horizontal(g218,g149)
    c: Vertical(g165,g134)
    c: Horizontal(g165,g147)
    c: Horizontal(g148,g167)
    c: Vertical(g135,g165)
    c: Equal(g155,g156)
    c: Equal(g156,g157)
    c: Equal(g157,g169)
    c: Equal(g169,g158)
    c: Equal(g158,g159)
    c: Equal(g159,g160)
    c: Equal(g160,g170)
    c: Horizontal(g157,g169)
    c: Horizontal(g169,g158)
    c: PointOnObject(g169,g-2)
    c: Horizontal(g155,g170)
    c: Horizontal(g170,g160)
    c: PointOnObject(g170,g-2)
    c: Coincident(g183,g109)
    c: Coincident(g233,g234)
    c: Coincident(g234,g235)
    c: Coincident(g235,g236)
    c: Coincident(g236,g233)
    c: Horizontal(g233)
    c: Horizontal(g235)
    c: Vertical(g234)
    c: Vertical(g236)
    c: Coincident(g237,g238)
    c: Coincident(g238,g239)
    c: Coincident(g239,g240)
    c: Coincident(g240,g237)
    c: Horizontal(g237)
    c: Horizontal(g239)
    c: Vertical(g238)
    c: Vertical(g240)
    c: Coincident(g241,g242)
    c: Coincident(g242,g243)
    c: Coincident(g243,g244)
    c: Coincident(g244,g241)
    c: Horizontal(g241)
    c: Horizontal(g243)
    c: Vertical(g242)
    c: Vertical(g244)
    c: Coincident(g245,g246)
    c: Coincident(g246,g247)
    c: Coincident(g247,g248)
    c: Coincident(g248,g245)
    c: Horizontal(g245)
    c: Horizontal(g247)
    c: Vertical(g246)
    c: Vertical(g248)
    c: Coincident(g249,g250)
    c: Coincident(g250,g251)
    c: Coincident(g251,g252)
    c: Coincident(g252,g249)
    c: Horizontal(g249)
    c: Horizontal(g251)
    c: Vertical(g250)
    c: Vertical(g252)
    c: Coincident(g253,g254)
    c: Coincident(g254,g255)
    c: Coincident(g255,g256)
    c: Coincident(g256,g253)
    c: Horizontal(g253)
    c: Horizontal(g255)
    c: Vertical(g254)
    c: Vertical(g256)
    c: Coincident(g257,g258)
    c: Coincident(g258,g259)
    c: Coincident(g259,g260)
    c: Coincident(g260,g257)
    c: Horizontal(g257)
    c: Horizontal(g259)
    c: Vertical(g258)
    c: Vertical(g260)
    c: Coincident(g261,g262)
    c: Coincident(g262,g263)
    c: Coincident(g263,g264)
    c: Coincident(g264,g261)
    c: Horizontal(g261)
    c: Horizontal(g263)
    c: Vertical(g262)
    c: Vertical(g264)
    c: Coincident(g265,g266)
    c: Coincident(g266,g267)
    c: Coincident(g267,g268)
    c: Coincident(g268,g265)
    c: Horizontal(g265)
    c: Horizontal(g267)
    c: Vertical(g266)
    c: Vertical(g268)
    c: Vertical(g183,g241)
    c: DistanceY(g244,g244) = 13.95
    c: Vertical(g241,g110)
    c: Horizontal(g243,g5)
    c: Horizontal(g245,g241)
    c: Vertical(g113,g245)
    c: Vertical(g112,g245)
    c: Vertical(g117,g257)
    c: Vertical(g116,g257)
    c: Horizontal(g245,g257)
    c: Horizontal(g242,g247)
    c: Horizontal(g246,g259)
    c: DistanceY(g233,g152) = 6
    c: Horizontal(g233,g237)
    c: Horizontal(g127,g237)
    c: DistanceX(g121,g1) = 30
    c: Horizontal(g128,g238)
    c: Horizontal(g239,g234)
    c: Vertical(g142,g233)
    c: Vertical(g143,g233)
    c: Vertical(g237,g149)
    c: Vertical(g148,g237)
    c: Vertical(g249,g119)
    c: Vertical(g249,g119)
    c: Vertical(g267,g123)
    c: Vertical(g266,g123)
    c: Horizontal(g249,g267)
    c: Horizontal(g265,g251)
    c: Vertical(g255,g250)
    c: Vertical(g254,g251)
    c: Vertical(g263,g265)
    c: Vertical(g262,g265)
    c: Horizontal(g263,g254)
    c: Horizontal(g266,g135)
    c: Horizontal(g265,g133)
    c: Horizontal(g262,g162)
    c: Horizontal(g261,g161)
    c: Horizontal(g253,g261)
    c: Coincident(g269,g270)
    c: Coincident(g270,g271)
    c: Coincident(g271,g272)
    c: Coincident(g272,g269)
    c: Horizontal(g269)
    c: Horizontal(g271)
    c: Vertical(g270)
    c: Vertical(g272)
    c: Coincident(g273,g274)
    c: Coincident(g274,g275)
    c: Coincident(g275,g276)
    c: Coincident(g276,g273)
    c: Horizontal(g273)
    c: Horizontal(g275)
    c: Vertical(g274)
    c: Vertical(g276)
    c: Coincident(g277,g278)
    c: Coincident(g278,g279)
    c: Coincident(g279,g280)
    c: Coincident(g280,g277)
    c: Horizontal(g277)
    c: Horizontal(g279)
    c: Vertical(g278)
    c: Vertical(g280)
    c: Horizontal(g269,g273)
    c: Horizontal(g273,g277)
    c: Horizontal(g270,g275)
    c: Horizontal(g274,g279)
    c: Horizontal(g269,g257)
    c: Horizontal(g271,g258)
    c: Vertical(g278,g253)
    c: Vertical(g279,g253)
    c: Vertical(g274,g261)
    c: Vertical(g275,g261)
    c: Vertical(g270,g127)
    c: Vertical(g271,g127)
    c: Coincident(g281,g282)
    c: Coincident(g282,g283)
    c: Coincident(g283,g284)
    c: Coincident(g284,g281)
    c: Horizontal(g281)
    c: Horizontal(g283)
    c: Vertical(g282)
    c: Vertical(g284)
    c: Vertical(g281,g219)
    c: Horizontal(g283,g222)
    c: Vertical(g281,g218)
    c: Horizontal(g151,g281)
    c: Coincident(g285,g286)
    c: Coincident(g286,g287)
    c: Coincident(g287,g288)
    c: Coincident(g288,g285)
    c: Horizontal(g285)
    c: Horizontal(g287)
    c: Vertical(g286)
    c: Vertical(g288)
    c: Horizontal(g285,g151)
    c: DistanceX(g151,g285) = 12
    c: Horizontal(g152,g287)
    c: DistanceX(g285,g285) = 13.95
    c: Coincident(g289,g290)
    c: Coincident(g290,g291)
    c: Coincident(g291,g292)
    c: Coincident(g292,g289)
    c: Horizontal(g289)
    c: Horizontal(g291)
    c: Vertical(g290)
    c: Vertical(g292)
    c: PointOnObject(g290,g-2)
    c: Coincident(g293,g294)
    c: Coincident(g294,g295)
    c: Coincident(g295,g296)
    c: Coincident(g296,g293)
    c: Horizontal(g293)
    c: Horizontal(g295)
    c: Vertical(g294)
    c: Vertical(g296)
    c: PointOnObject(g294,g-2)
    c: Coincident(g297,g298)
    c: Coincident(g298,g299)
    c: Coincident(g299,g300)
    c: Coincident(g300,g297)
    c: Horizontal(g297)
    c: Horizontal(g299)
    c: Vertical(g298)
    c: Vertical(g300)
    c: PointOnObject(g298,g-2)
    c: Coincident(g301,g302)
    c: Coincident(g302,g303)
    c: Coincident(g303,g304)
    c: Coincident(g304,g301)
    c: Horizontal(g301)
    c: Horizontal(g303)
    c: Vertical(g302)
    c: Vertical(g304)
    c: PointOnObject(g302,g-2)
    c: Coincident(g305,g306)
    c: Coincident(g306,g307)
    c: Coincident(g307,g308)
    c: Coincident(g308,g305)
    c: Horizontal(g305)
    c: Horizontal(g307)
    c: Vertical(g306)
    c: Vertical(g308)
    c: PointOnObject(g306,g-2)
    c: Horizontal(g289,g73)
    c: Horizontal(g293,g85)
    c: Horizontal(g75,g290)
    c: Vertical(g291,g293)
    c: DistanceX(g289,g289) = 13.95
    c: Vertical(g295,g297)
    c: Horizontal(g294,g86)
    c: Horizontal(g297,g97)
    c: Horizontal(g298,g99)
    c: Horizontal(g301,g109)
    c: Horizontal(g302,g183)
    c: DistanceY(g305,g302) = 6
    c: Vertical(g299,g301)
    c: Vertical(g305,g303)
    c: DistanceY(g308,g308) = 13.95
FEATURE [Spreadsheet::Sheet] Spreadsheet
  cells = A1=key_spacing; B1(key_spacing)=6; A2=group_spacing; B2(group_spacing)=12; A3=key_size; B3(key_size)=13.95
FEATURE [PartDesign::Pad] Pad
  Direction = (0,0,1)
  Length = 1.5
  Length2 = 100
  Profile = -> Sketch
  Type = 0
FEATURE [PartDesign::Body] Body
  Group = -> [Sketch,Pad]
  Origin = -> Origin
  Tip = -> Pad
